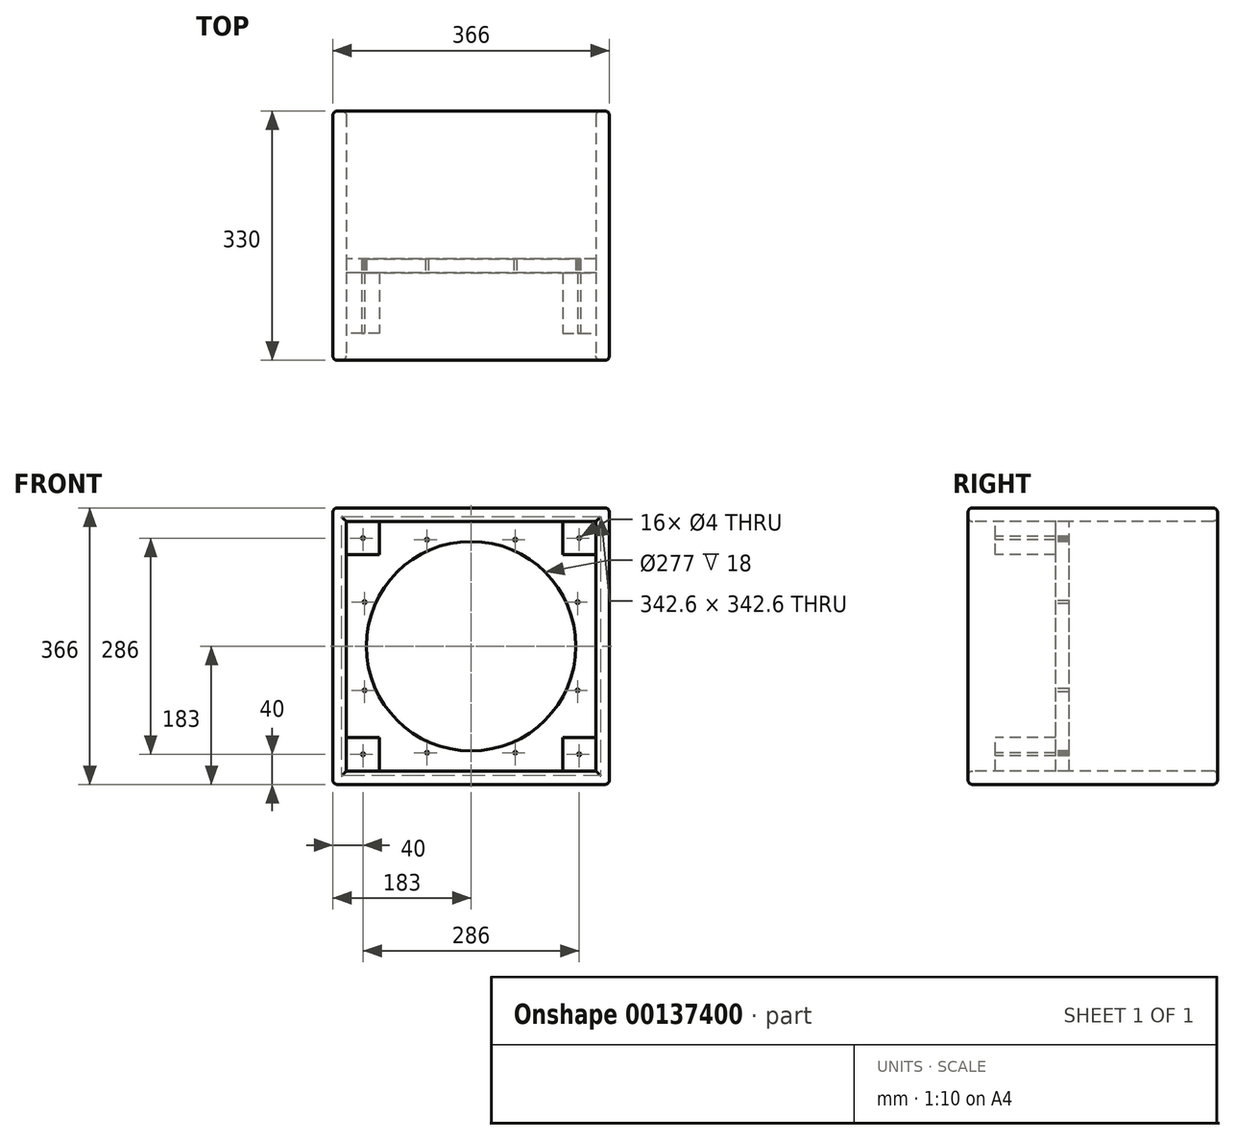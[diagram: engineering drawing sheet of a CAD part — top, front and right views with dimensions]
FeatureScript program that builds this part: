
annotation { "Feature Type Name" : "Feature", "Feature Type Description" : "" }
export const myFeature = defineFeature(function(context is Context, id is Id, definition is map)
    precondition{}
    {
        {
            var Q0;
            Q0=qCreatedBy(makeId("Front.planeOp"),FACE);
            var sketch = newSketch(context, id + "F0", { "sketchPlane" : qUnion([Q0])});
            skCircle(sketch, "E0", {"center": v(0, 0) * mm, "radius": 157.5 * mm, "construction": true});
            skLineSegment(sketch, "E1.bottom", {"start": v(165, -165) * mm, "end": v(-165, -165) * mm});
            skLineSegment(sketch, "E1.top", {"start": v(165, 165) * mm, "end": v(-165, 165) * mm});
            skLineSegment(sketch, "E1.left", {"start": v(165, -165) * mm, "end": v(165, 165) * mm});
            skLineSegment(sketch, "E1.right", {"start": v(-165, -165) * mm, "end": v(-165, 165) * mm});
            skCircle(sketch, "E2", {"center": v(0, 0) * mm, "radius": 138.5 * mm});
            skLineSegment(sketch, "E3", {"start": v(-121, 165) * mm, "end": v(-121, 121) * mm});
            skLineSegment(sketch, "E4", {"start": v(-121, 121) * mm, "end": v(-165, 121) * mm});
            skLineSegment(sketch, "E5.bottom", {"start": v(183, 183) * mm, "end": v(-183, 183) * mm});
            skLineSegment(sketch, "E5.top", {"start": v(183, -183) * mm, "end": v(-183, -183) * mm});
            skLineSegment(sketch, "E5.left", {"start": v(183, 183) * mm, "end": v(183, -183) * mm});
            skLineSegment(sketch, "E5.right", {"start": v(-183, 183) * mm, "end": v(-183, -183) * mm});
            skCircle(sketch, "E6", {"center": v(-143, 143) * mm, "radius": 2 * mm});
            skLineSegment(sketch, "E7", {"start": v(0, 249.38) * mm, "end": v(0, -250.05) * mm, "construction": true});
            skPoint(sketch, "E7.endSnap0", {"position": v(0, -183) * mm});
            skLineSegment(sketch, "E8", {"start": v(-262.49, 0) * mm, "end": v(219.47, 0) * mm, "construction": true});
            skPoint(sketch, "E8.endSnap0", {"position": v(183, 0) * mm});
            skLineSegment(sketch, "E9.MirrorCS", {"start": v(121, 165) * mm, "end": v(121, 121) * mm});
            skLineSegment(sketch, "E10.MirrorCS", {"start": v(121, 121) * mm, "end": v(165, 121) * mm});
            skLineSegment(sketch, "E11.MirrorCS", {"start": v(121, -121) * mm, "end": v(165, -121) * mm});
            skLineSegment(sketch, "E12.MirrorCS", {"start": v(121, -165) * mm, "end": v(121, -121) * mm});
            skLineSegment(sketch, "E13.MirrorCS", {"start": v(-121, -165) * mm, "end": v(-121, -121) * mm});
            skLineSegment(sketch, "E14.MirrorCS", {"start": v(-121, -121) * mm, "end": v(-165, -121) * mm});
            skLineSegment(sketch, "E15", {"start": v(-121, 165) * mm, "end": v(-165, 121) * mm, "construction": true});
            skLineSegment(sketch, "E16", {"start": v(-165, 165) * mm, "end": v(-121, 121) * mm, "construction": true});
            skCircle(sketch, "E17.MirrorC", {"center": v(143, 143) * mm, "radius": 2 * mm});
            skCircle(sketch, "E18.MirrorC", {"center": v(143, -143) * mm, "radius": 2 * mm});
            skCircle(sketch, "E19.MirrorC", {"center": v(-143, -143) * mm, "radius": 2 * mm});
            skCircle(sketch, "E20", {"center": v(0, 0) * mm, "radius": 152.5 * mm, "construction": true});
            skLineSegment(sketch, "E21", {"start": v(0, 0) * mm, "end": v(162.52, 67.32) * mm, "construction": true});
            skCircle(sketch, "E22", {"center": v(140.9, 58.36) * mm, "radius": 2 * mm});
            skCircle(sketch, "E23.1.0", {"center": v(58.36, 140.9) * mm, "radius": 2 * mm});
            skCircle(sketch, "E23.2.0", {"center": v(-58.36, 140.9) * mm, "radius": 2 * mm});
            skCircle(sketch, "E23.3.0", {"center": v(-140.9, 58.36) * mm, "radius": 2 * mm});
            skCircle(sketch, "E23.4.0", {"center": v(-140.9, -58.36) * mm, "radius": 2 * mm});
            skCircle(sketch, "E23.5.0", {"center": v(-58.36, -140.9) * mm, "radius": 2 * mm});
            skCircle(sketch, "E23.6.0", {"center": v(58.36, -140.9) * mm, "radius": 2 * mm});
            skCircle(sketch, "E23.7.0", {"center": v(140.9, -58.36) * mm, "radius": 2 * mm});
            skSolve(sketch);
        }
        {
            var Q0;
            {var subQ5=sQuery(id+"F0.wireOp",EDGE,"E1.bottom");Q0=makeQuery(id+"F0.imprint","IMPRINT",FACE,{"disambiguationData":[TD([[makeQuery(id+"F0.imprint","IMPRINT",EDGE,{"derivedFrom":subQ5}),1.0]])]});}
            extrude(context, id + "F1", {"entities" : qUnion([Q0]), "oppositeDirection" : true, "depth" : 330 * mm});
        }
        {
            var Q0;
            {var subQ1=sQuery(id+"F0.wireOp",EDGE,"E1.bottom");Q0=makeQuery(id+"F0.imprint","IMPRINT",FACE,{"disambiguationData":[TD([[makeQuery(id+"F0.imprint","IMPRINT",EDGE,{"derivedFrom":subQ1}),-1.0]])]});}
            var Q1;
            {var subQ3=sQuery(id+"F0.wireOp",EDGE,"E3");Q1=makeQuery(id+"F0.imprint","IMPRINT",FACE,{"disambiguationData":[TD([[makeQuery(id+"F0.imprint","IMPRINT",EDGE,{"derivedFrom":subQ3}),-1.0]])]});}
            var Q2;
            Q2=makeQuery(id+"F0.imprint","IMPRINT",FACE,{"disambiguationData":[TD([[makeQuery(id+"F0.imprint","IMPRINT",EDGE,{"derivedFrom":sQuery(id+"F0.wireOp",EDGE,"E2")}),-1.0]])]});
            var Q3;
            {var subQ4=sQuery(id+"F0.wireOp",EDGE,"E9.MirrorCS");Q3=makeQuery(id+"F0.imprint","IMPRINT",FACE,{"disambiguationData":[TD([[makeQuery(id+"F0.imprint","IMPRINT",EDGE,{"derivedFrom":subQ4}),1.0]])]});}
            extrude(context, id + "F2", {"entities" : qUnion([Q0, Q1, Q2, Q3]), "oppositeDirection" : true, "depth" : 18 * mm});
        }
        {
            var Q0;
            {var subQ3=sQuery(id+"F0.wireOp",EDGE,"E3");Q0=makeQuery(id+"F0.imprint","IMPRINT",FACE,{"disambiguationData":[TD([[makeQuery(id+"F0.imprint","IMPRINT",EDGE,{"derivedFrom":subQ3}),-1.0]])]});}
            var Q1;
            {var subQ4=sQuery(id+"F0.wireOp",EDGE,"E9.MirrorCS");Q1=makeQuery(id+"F0.imprint","IMPRINT",FACE,{"disambiguationData":[TD([[makeQuery(id+"F0.imprint","IMPRINT",EDGE,{"derivedFrom":subQ4}),1.0]])]});}
            var Q2;
            {var subQ0=sQuery(id+"F0.wireOp",EDGE,"E11.MirrorCS");Q2=makeQuery(id+"F0.imprint","IMPRINT",FACE,{"disambiguationData":[TD([[makeQuery(id+"F0.imprint","IMPRINT",EDGE,{"derivedFrom":subQ0}),-1.0]])]});}
            var Q3;
            {var subQ1=sQuery(id+"F0.wireOp",EDGE,"E13.MirrorCS");Q3=makeQuery(id+"F0.imprint","IMPRINT",FACE,{"disambiguationData":[TD([[makeQuery(id+"F0.imprint","IMPRINT",EDGE,{"derivedFrom":subQ1}),1.0]])]});}
            extrude(context, id + "F3", {"entities" : qUnion([Q0, Q1, Q2, Q3]), "oppositeDirection" : true, "depth" : 80 * mm});
        }
        {
            var Q0;
            Q0=makeQuery(id+"F1.opExtrude","SWEPT_FACE",FACE,{"disambiguationData":[OSD([sQuery(id+"F0.wireOp",EDGE,"E5.left")])]});
            var Q1;
            Q1=makeQuery(id+"F1.opExtrude","SWEPT_FACE",FACE,{"disambiguationData":[OSD([sQuery(id+"F0.wireOp",EDGE,"E5.bottom")])]});
            var Q2;
            Q2=makeQuery(id+"F1.opExtrude","SWEPT_FACE",FACE,{"disambiguationData":[OSD([sQuery(id+"F0.wireOp",EDGE,"E5.right")])]});
            var Q3;
            Q3=makeQuery(id+"F1.opExtrude","SWEPT_FACE",FACE,{"disambiguationData":[OSD([sQuery(id+"F0.wireOp",EDGE,"E5.top")])]});
            var Q4;
            Q4=makeQuery(id+"F1.opExtrude","CAP_FACE",FACE,{"disambiguationData":[OSD([sQuery(id+"F0.wireOp",EDGE,"E1.bottom"),sQuery(id+"F0.wireOp",EDGE,"E1.top"),sQuery(id+"F0.wireOp",EDGE,"E1.left"),sQuery(id+"F0.wireOp",EDGE,"E1.right"),sQuery(id+"F0.wireOp",EDGE,"E5.bottom"),sQuery(id+"F0.wireOp",EDGE,"E5.top"),sQuery(id+"F0.wireOp",EDGE,"E5.left"),sQuery(id+"F0.wireOp",EDGE,"E5.right")])],"isStart":true});
            var Q5;
            Q5=makeQuery(id+"F1.opExtrude","CAP_FACE",FACE,{"disambiguationData":[OSD([sQuery(id+"F0.wireOp",EDGE,"E1.bottom"),sQuery(id+"F0.wireOp",EDGE,"E1.top"),sQuery(id+"F0.wireOp",EDGE,"E1.left"),sQuery(id+"F0.wireOp",EDGE,"E1.right"),sQuery(id+"F0.wireOp",EDGE,"E5.bottom"),sQuery(id+"F0.wireOp",EDGE,"E5.top"),sQuery(id+"F0.wireOp",EDGE,"E5.left"),sQuery(id+"F0.wireOp",EDGE,"E5.right")])],"isStart":false});
            fillet(context, id + "F4", {"entities" : qUnion([Q0, Q1, Q2, Q3, Q4, Q5]), "radius" : 6.3 * mm, "tangentPropagation" : true, "allowEdgeOverflow" : false});
        }
        {
            var Q0;
            Q0=makeQuery(id+"F3.opExtrude","SWEPT_BODY",BODY,{"disambiguationData":[OSD([sQuery(id+"F0.wireOp",EDGE,"E1.top"),sQuery(id+"F0.wireOp",EDGE,"E1.right"),sQuery(id+"F0.wireOp",EDGE,"E3"),sQuery(id+"F0.wireOp",EDGE,"E4")])]});
            var Q1;
            Q1=makeQuery(id+"F3.opExtrude","SWEPT_BODY",BODY,{"disambiguationData":[OSD([sQuery(id+"F0.wireOp",EDGE,"E1.top"),sQuery(id+"F0.wireOp",EDGE,"E1.left"),sQuery(id+"F0.wireOp",EDGE,"E9.MirrorCS"),sQuery(id+"F0.wireOp",EDGE,"E10.MirrorCS"),sQuery(id+"F0.wireOp",EDGE,"E17.MirrorC")])]});
            var Q2;
            Q2=makeQuery(id+"F3.opExtrude","SWEPT_BODY",BODY,{"disambiguationData":[OSD([sQuery(id+"F0.wireOp",EDGE,"E1.bottom"),sQuery(id+"F0.wireOp",EDGE,"E1.left"),sQuery(id+"F0.wireOp",EDGE,"E11.MirrorCS"),sQuery(id+"F0.wireOp",EDGE,"E12.MirrorCS"),sQuery(id+"F0.wireOp",EDGE,"E18.MirrorC")])]});
            var Q3;
            Q3=makeQuery(id+"F3.opExtrude","SWEPT_BODY",BODY,{"disambiguationData":[OSD([sQuery(id+"F0.wireOp",EDGE,"E1.bottom"),sQuery(id+"F0.wireOp",EDGE,"E1.right"),sQuery(id+"F0.wireOp",EDGE,"E13.MirrorCS"),sQuery(id+"F0.wireOp",EDGE,"E14.MirrorCS"),sQuery(id+"F0.wireOp",EDGE,"E19.MirrorC")])]});
            var Q4;
            {var subQ0=sQuery(id+"F0.wireOp",EDGE,"E5.right");Q4=makeQuery(id+"F4.opFillet","BLEND_EDGE",EDGE,{"blendedFrom":[makeQuery(id+"F1.opExtrude","SWEPT_EDGE",EDGE,{"disambiguationData":[OSD([sQuery(id+"F0.wireOp",EDGE,"E5.bottom"),subQ0])]}),makeQuery(id+"F1.opExtrude","SWEPT_FACE",FACE,{"disambiguationData":[OSD([subQ0])]})],"blendedInto":[makeQuery(id+"F1.opExtrude","SWEPT_FACE",FACE,{"disambiguationData":[OSD([subQ0])]})]});}
            transform(context, id + "F5", {"entities" : qUnion([Q0, Q1, Q2, Q3]), "transformType" : TransformType.TRANSLATION_DISTANCE, "transformDirection" : qUnion([Q4]), "distance" : 36 * mm, "makeCopy" : false});
        }
        {
            var Q0;
            Q0=makeQuery(id+"F2.opExtrude","SWEPT_BODY",BODY,{"disambiguationData":[OSD([sQuery(id+"F0.wireOp",EDGE,"E1.bottom"),sQuery(id+"F0.wireOp",EDGE,"E1.top"),sQuery(id+"F0.wireOp",EDGE,"E1.left"),sQuery(id+"F0.wireOp",EDGE,"E1.right"),sQuery(id+"F0.wireOp",EDGE,"E2")])]});
            var Q1;
            {var subQ0=sQuery(id+"F0.wireOp",EDGE,"E5.right");Q1=makeQuery(id+"F4.opFillet","BLEND_EDGE",EDGE,{"blendedFrom":[makeQuery(id+"F1.opExtrude","SWEPT_EDGE",EDGE,{"disambiguationData":[OSD([sQuery(id+"F0.wireOp",EDGE,"E5.bottom"),subQ0])]}),makeQuery(id+"F1.opExtrude","SWEPT_FACE",FACE,{"disambiguationData":[OSD([subQ0])]})],"blendedInto":[makeQuery(id+"F1.opExtrude","SWEPT_FACE",FACE,{"disambiguationData":[OSD([subQ0])]})]});}
            transform(context, id + "F6", {"entities" : qUnion([Q0]), "transformType" : TransformType.TRANSLATION_DISTANCE, "transformDirection" : qUnion([Q1]), "distance" : (36 + 80) * mm, "makeCopy" : false});
        }
    });
